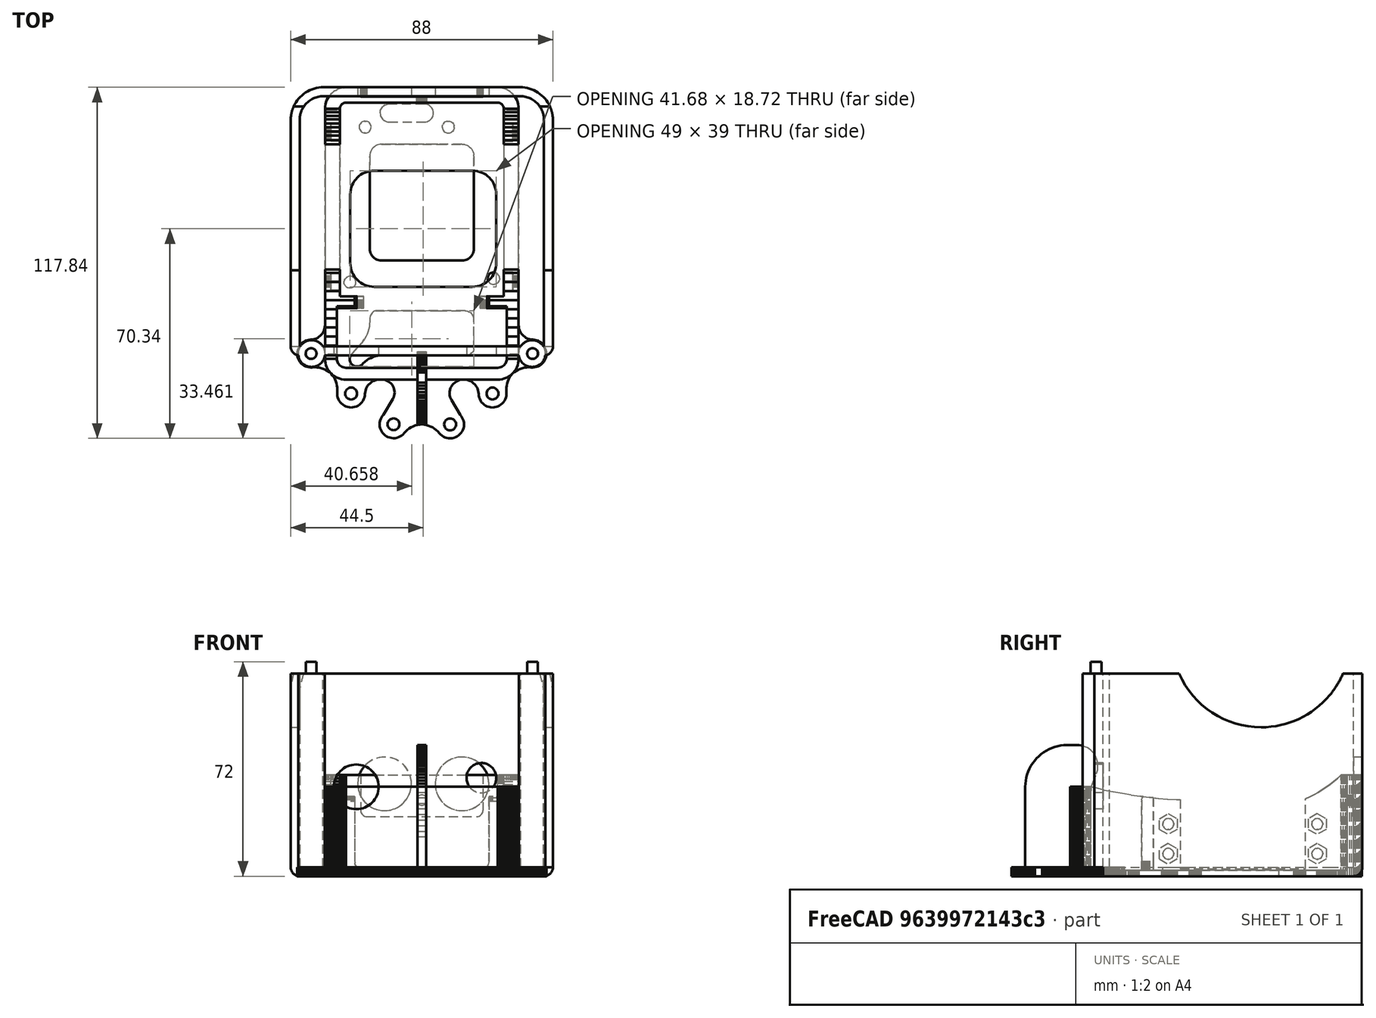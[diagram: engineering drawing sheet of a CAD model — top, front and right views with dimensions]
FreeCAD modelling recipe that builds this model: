
FCSTD DOCUMENT  (FreeCAD 0.14R3702 (Git))
Label: carcasa
License: CC-BY 3.0
LicenseURL: http://creativecommons.org/licenses/by/3.0/
objects: Part::Cylinder×9, Part::Cut×6, Part::Feature×3, Part::Box×2, Part::Fillet×2, Part::MultiFuse×2, Part::Thickness×1, Mesh::Feature×1
note: 25 computed .brp shape members not serialized (recipe doc carries the construction recipe); baked Part::Feature solids carry a one-line shape summary decoded from their .brp

FEATURE [Part::Feature] _xChasis001
  shape: bbox 83.67 x 117.7 x 44 mm, 6070 faces, 0 solids (baked)
FEATURE [Part::Feature] _xChasis001_solid  label="_xChasis001 (Solid)"
  shape: bbox 83.67 x 117.7 x 44 mm, 6070 faces (baked)
FEATURE [Part::Feature] _xChasis001_solid001  label="_xChasis001 (Solid)001"
  shape: bbox 83.67 x 117.7 x 44 mm, 1543 faces (baked)
FEATURE [Part::Cylinder] Cylinder  label="Cilindro"
  Angle = 360
  Height = 68
  Placement = pos=(-37,-30.4,-68) rot=(0,0,1;0rad)
  Radius = 4.5
FEATURE [Part::Cylinder] Cylinder001  label="Cilindro001"
  Angle = 360
  Height = 68
  Placement = pos=(37,-30.4,-68) rot=(0,0,1;0rad)
  Radius = 4.5
FEATURE [Part::Box] Box  label="Cubo"
  Height = 65
  Length = 82
  Placement = pos=(-41,-28,-65) rot=(0,0,1;0rad)
  Width = 84
FEATURE [Part::Fillet] Fillet
  Base = -> Box
  Edges = 2 edges r=8: [Edge3,Edge7]
FEATURE [Part::Thickness] Thickness
  Faces = -> Fillet [Face2]
  Intersection = false
  Join = 0
  Mode = 0
  SelfIntersection = false
  Value = 3
FEATURE [Part::MultiFuse] Fusion
  Shapes = -> [Cylinder001,Cylinder,Thickness]
FEATURE [Part::Cylinder] Cylinder002  label="Cilindro002"
  Angle = 360
  Height = 4
  Placement = pos=(-37.17,-30.4,0) rot=(0,0,1;0rad)
  Radius = 1.8
FEATURE [Part::Cylinder] Cylinder003  label="Cilindro003"
  Angle = 360
  Height = 4
  Placement = pos=(37.18,-30.4,0) rot=(0,0,1;0rad)
  Radius = 1.8
FEATURE [Part::MultiFuse] Fusion001
  Shapes = -> [Fusion,Cylinder002,Cylinder003]
FEATURE [Part::Cylinder] Cylinder004  label="Cilindro004"
  Angle = 360
  Height = 100
  Placement = pos=(-51,25,12) rot=(0,1,0;1.5708rad)
  Radius = 30
FEATURE [Part::Cut] Cut  label="carcasa"
  Base = -> Fusion001
  Placement = pos=(0,0,68) rot=(0,0,1;0rad)
  Tool = -> Cylinder004
FEATURE [Mesh::Feature] hc_sr  label="hc-sr04"
  Placement = pos=(23,55,21) rot=(0,0.707107,0.707107;3.14159rad)
FEATURE [Part::Cylinder] Cylinder005  label="Cilindro005"
  Angle = 360
  Height = 10
  Placement = pos=(-12.5,62,31) rot=(1,0,0;1.5708rad)
  Radius = 9
FEATURE [Part::Cylinder] Cylinder006  label="Cilindro006"
  Angle = 360
  Height = 10
  Placement = pos=(13.5,62,31) rot=(1,0,0;1.5708rad)
  Radius = 9
FEATURE [Part::Cut] Cut001
  Base = -> Cut
  Tool = -> Cylinder006
FEATURE [Part::Cut] Cut002
  Base = -> Cut001
  Tool = -> Cylinder005
FEATURE [Part::Box] Box001  label="Cubo001"
  Height = 10
  Length = 49
  Placement = pos=(-24,-8,-3) rot=(0,0,1;0rad)
  Width = 39
FEATURE [Part::Fillet] Fillet001
  Base = -> Box001
  Edges = 4 edges r=8: [Edge1,Edge3,Edge5,Edge7]
FEATURE [Part::Cut] Cut003  label="carcasa001"
  Base = -> Cut002
  Tool = -> Fillet001
FEATURE [Part::Cylinder] Cylinder007  label="Cilindro007"
  Angle = 360
  Height = 10
  Placement = pos=(-22,-26,30) rot=(1,0,0;1.5708rad)
  Radius = 7.5
FEATURE [Part::Cut] Cut004
  Base = -> Cut003
  Tool = -> Cylinder007
FEATURE [Part::Cylinder] Cylinder008  label="Cilindro008"
  Angle = 360
  Height = 10
  Placement = pos=(20,-26,33) rot=(1,0,0;1.5708rad)
  Radius = 5
FEATURE [Part::Cut] Cut005
  Base = -> Cut004
  Tool = -> Cylinder008
